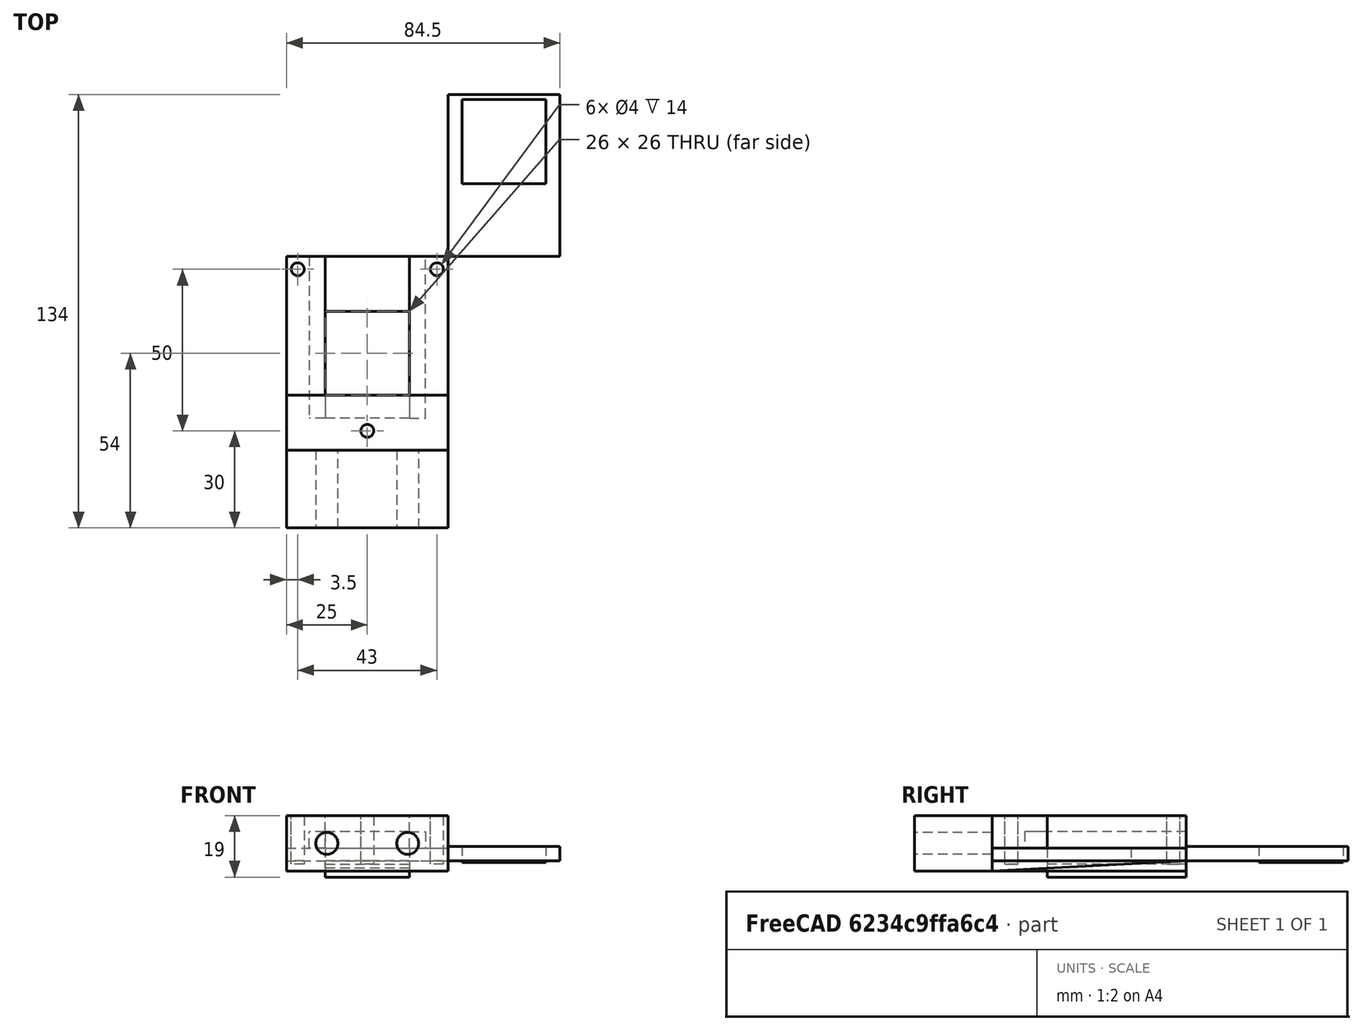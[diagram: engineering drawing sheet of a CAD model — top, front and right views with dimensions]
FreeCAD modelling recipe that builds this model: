
FCSTD DOCUMENT  (FreeCAD 0.15R4671 (Git))
Label: CageTubeConnector
License: All rights reserved
LicenseURL: http://en.wikipedia.org/wiki/All_rights_reserved
objects: Sketcher::SketchObject×22, PartDesign::Pocket×13, PartDesign::Pad×7, Mesh::Feature×2
note: 62 computed .brp shape members not serialized (recipe doc carries the construction recipe); baked Part::Feature solids carry a one-line shape summary decoded from their .brp

FEATURE [Sketcher::SketchObject] Sketch
  sketch-geometry (4):
    g0: LineSegment StartX=-50 StartY=0 StartZ=0 EndX=0 EndY=0 EndZ=0
    g1: LineSegment StartX=0 StartY=0 StartZ=0 EndX=0 EndY=-60 EndZ=0
    g2: LineSegment StartX=0 StartY=-60 StartZ=0 EndX=-50 EndY=-60 EndZ=0
    g3: LineSegment StartX=-50 StartY=-60 StartZ=0 EndX=-50 EndY=0 EndZ=0
  constraints (11):
    c: Coincident(g0,g1)
    c: Coincident(g1,g2)
    c: Coincident(g2,g3)
    c: Coincident(g3,g0)
    c: Horizontal(g0)
    c: Horizontal(g2)
    c: Vertical(g1)
    c: Vertical(g3)
    c: Distance(g0) = 50
    c: Distance(g1) = 60
    c: Coincident(g0,g-1)
FEATURE [PartDesign::Pad] Pad
  Length = 4
  Length2 = 100
  Sketch = -> Sketch
  Type = 0
FEATURE [Sketcher::SketchObject] Sketch001
  Placement = pos=(0,0,4) rot=(0,0,1;0rad)
  Support = -> Pad [Face6]
  sketch-geometry (4):
    g0: LineSegment StartX=-38 StartY=-17 StartZ=0 EndX=-12 EndY=-17 EndZ=0
    g1: LineSegment StartX=-12 StartY=-17 StartZ=0 EndX=-12 EndY=-43 EndZ=0
    g2: LineSegment StartX=-12 StartY=-43 StartZ=0 EndX=-38 EndY=-43 EndZ=0
    g3: LineSegment StartX=-38 StartY=-43 StartZ=0 EndX=-38 EndY=-17 EndZ=0
  constraints (12):
    c: Coincident(g0,g1)
    c: Coincident(g1,g2)
    c: Coincident(g2,g3)
    c: Coincident(g3,g0)
    c: Horizontal(g0)
    c: Horizontal(g2)
    c: Vertical(g1)
    c: Vertical(g3)
    c: Distance(g0) = 26
    c: DistanceX(g-1,g0) = -12
    c: Distance(g3) = 26
    c: DistanceY(g-1,g0) = -17
FEATURE [PartDesign::Pocket] Pocket
  Length = 5
  Sketch = -> Sketch001
  Type = 0
FEATURE [Sketcher::SketchObject] Sketch002
  Placement = pos=(0,0,4) rot=(0,0,1;0rad)
  Support = -> Pocket [Face5]
FEATURE [Sketcher::SketchObject] Sketch003
  Placement = pos=(0,0,4) rot=(0,0,1;0rad)
  Support = -> Pocket [Face5]
  sketch-geometry (4):
    g0: LineSegment StartX=-50 StartY=-43 StartZ=0 EndX=0 EndY=-43 EndZ=0
    g1: LineSegment StartX=0 StartY=-43 StartZ=0 EndX=0 EndY=-60 EndZ=0
    g2: LineSegment StartX=0 StartY=-60 StartZ=0 EndX=-50 EndY=-60 EndZ=0
    g3: LineSegment StartX=-50 StartY=-60 StartZ=0 EndX=-50 EndY=-43 EndZ=0
  constraints (12):
    c: Coincident(g0,g1)
    c: Coincident(g1,g2)
    c: Coincident(g2,g3)
    c: Coincident(g3,g0)
    c: Horizontal(g0)
    c: Horizontal(g2)
    c: Vertical(g1)
    c: Vertical(g3)
    c: Distance(g0) = 50
    c: Distance(g3) = 17
    c: DistanceX(g-1,g0) = 0
    c: DistanceY(g-1,g0) = -43
FEATURE [PartDesign::Pad] Pad001
  Length = 10
  Length2 = 100
  Sketch = -> Sketch003
  Type = 0
FEATURE [Sketcher::SketchObject] Sketch004
  Placement = pos=(0,0,4) rot=(0,0,1;0rad)
  Support = -> Pad001 [Face5]
  sketch-geometry (4):
    g0: LineSegment StartX=-50 StartY=0 StartZ=0 EndX=-38 EndY=0 EndZ=0
    g1: LineSegment StartX=-38 StartY=0 StartZ=0 EndX=-38 EndY=-43 EndZ=0
    g2: LineSegment StartX=-38 StartY=-43 StartZ=0 EndX=-50 EndY=-43 EndZ=0
    g3: LineSegment StartX=-50 StartY=-43 StartZ=0 EndX=-50 EndY=0 EndZ=0
  constraints (12):
    c: Coincident(g0,g1)
    c: Coincident(g1,g2)
    c: Coincident(g2,g3)
    c: Coincident(g3,g0)
    c: Horizontal(g0)
    c: Horizontal(g2)
    c: Vertical(g1)
    c: Vertical(g3)
    c: Distance(g1) = 43
    c: Distance(g0) = 12
    c: DistanceX(g-1,g0) = -38
    c: DistanceY(g0) = 0
FEATURE [PartDesign::Pad] Pad002
  Length = 10
  Length2 = 100
  Sketch = -> Sketch004
  Type = 0
FEATURE [Sketcher::SketchObject] Sketch005
  Placement = pos=(0,0,4) rot=(0,0,1;0rad)
  Support = -> Pad002 [Face11]
  sketch-geometry (4):
    g0: LineSegment StartX=-12 StartY=0 StartZ=0 EndX=0 EndY=0 EndZ=0
    g1: LineSegment StartX=0 StartY=0 StartZ=0 EndX=0 EndY=-43 EndZ=0
    g2: LineSegment StartX=0 StartY=-43 StartZ=0 EndX=-12 EndY=-43 EndZ=0
    g3: LineSegment StartX=-12 StartY=-43 StartZ=0 EndX=-12 EndY=0 EndZ=0
  constraints (12):
    c: Coincident(g0,g1)
    c: Coincident(g1,g2)
    c: Coincident(g2,g3)
    c: Coincident(g3,g0)
    c: Horizontal(g0)
    c: Horizontal(g2)
    c: Vertical(g1)
    c: Vertical(g3)
    c: Distance(g1) = 43
    c: Distance(g0) = 12
    c: DistanceX(g-1,g0) = 0
    c: DistanceY(g-1,g0) = 0
FEATURE [PartDesign::Pad] Pad003
  Length = 10
  Length2 = 100
  Sketch = -> Sketch005
  Type = 0
FEATURE [Sketcher::SketchObject] Sketch006
  Placement = pos=(-38,0,0) rot=(0.57735,0.57735,0.57735;2.0944rad)
  Support = -> Pad003 [Face18]
  sketch-geometry (4):
    g0: LineSegment StartX=0 StartY=9 StartZ=0 EndX=-50 EndY=9 EndZ=0
    g1: LineSegment StartX=-50 StartY=9 StartZ=0 EndX=-50 EndY=4 EndZ=0
    g2: LineSegment StartX=-50 StartY=4 StartZ=0 EndX=0 EndY=4 EndZ=0
    g3: LineSegment StartX=0 StartY=4 StartZ=0 EndX=0 EndY=9 EndZ=0
  constraints (12):
    c: Coincident(g0,g1)
    c: Coincident(g1,g2)
    c: Coincident(g2,g3)
    c: Coincident(g3,g0)
    c: Horizontal(g0)
    c: Horizontal(g2)
    c: Vertical(g1)
    c: Vertical(g3)
    c: Distance(g3) = 5
    c: Distance(g0) = 50
    c: DistanceX(g-1,g2) = 0
    c: DistanceY(g-1,g2) = 4
FEATURE [PartDesign::Pocket] Pocket001
  Length = 5
  Sketch = -> Sketch006
  Type = 0
FEATURE [Sketcher::SketchObject] Sketch007
  Placement = pos=(-12,0,0) rot=(0.57735,-0.57735,-0.57735;2.0944rad)
  Support = -> Pocket001 [Face20]
  sketch-geometry (4):
    g0: LineSegment StartX=0 StartY=4 StartZ=0 EndX=50 EndY=4 EndZ=0
    g1: LineSegment StartX=50 StartY=4 StartZ=0 EndX=50 EndY=9 EndZ=0
    g2: LineSegment StartX=50 StartY=9 StartZ=0 EndX=0 EndY=9 EndZ=0
    g3: LineSegment StartX=0 StartY=9 StartZ=0 EndX=0 EndY=4 EndZ=0
  constraints (12):
    c: Coincident(g0,g1)
    c: Coincident(g1,g2)
    c: Coincident(g2,g3)
    c: Coincident(g3,g0)
    c: Horizontal(g0)
    c: Horizontal(g2)
    c: Vertical(g1)
    c: Vertical(g3)
    c: Distance(g3) = 5
    c: Distance(g2) = 50
    c: DistanceY(g-1,g0) = 4
    c: DistanceX(g-1,g0) = 0
FEATURE [PartDesign::Pocket] Pocket002
  Length = 5
  Sketch = -> Sketch007
  Type = 0
FEATURE [Sketcher::SketchObject] Sketch008
  Placement = pos=(0,-43,0) rot=(0,0.707107,0.707107;3.14159rad)
  Support = -> Pocket002 [Face20]
  sketch-geometry (4):
    g0: LineSegment StartX=38 StartY=4 StartZ=0 EndX=12 EndY=4 EndZ=0
    g1: LineSegment StartX=12 StartY=4 StartZ=0 EndX=12 EndY=9 EndZ=0
    g2: LineSegment StartX=12 StartY=9 StartZ=0 EndX=38 EndY=9 EndZ=0
    g3: LineSegment StartX=38 StartY=9 StartZ=0 EndX=38 EndY=4 EndZ=0
  constraints (12):
    c: Coincident(g0,g1)
    c: Coincident(g1,g2)
    c: Coincident(g2,g3)
    c: Coincident(g3,g0)
    c: Horizontal(g0)
    c: Horizontal(g2)
    c: Vertical(g1)
    c: Vertical(g3)
    c: Distance(g3) = 5
    c: Distance(g0) = 26
    c: DistanceY(g-1,g0) = 4
    c: DistanceX(g-1,g0) = 12
FEATURE [PartDesign::Pocket] Pocket003
  Length = 7
  Sketch = -> Sketch008
  Type = 0
FEATURE [Sketcher::SketchObject] Sketch009
  Placement = pos=(0,0,14) rot=(0,0,1;0rad)
  Support = -> Pocket003 [Face31]
  sketch-geometry (1):
    g0: Circle CenterX=-25 CenterY=-54 CenterZ=0 NormalX=0 NormalY=0 NormalZ=1 Radius=2
  constraints (3):
    c: DistanceX(g-1,g0) = -25
    c: DistanceY(g-1,g0) = -54
    c: Radius(g0) = 2
FEATURE [PartDesign::Pocket] Pocket004
  Length = 15
  Sketch = -> Sketch009
  Type = 0
FEATURE [Sketcher::SketchObject] Sketch010
  Placement = pos=(0,0,14) rot=(0,0,1;0rad)
  Support = -> Pocket004 [Face26]
  sketch-geometry (1):
    g0: Circle CenterX=-46.5 CenterY=-4 CenterZ=0 NormalX=0 NormalY=0 NormalZ=1 Radius=2
  constraints (3):
    c: Radius(g0) = 2
    c: DistanceY(g-1,g0) = -4
    c: DistanceX(g-1,g0) = -46.5
FEATURE [PartDesign::Pocket] Pocket005
  Length = 15
  Sketch = -> Sketch010
  Type = 0
FEATURE [Sketcher::SketchObject] Sketch011
  Placement = pos=(0,0,14) rot=(0,0,1;0rad)
  Support = -> Pocket005 [Face31]
  sketch-geometry (1):
    g0: Circle CenterX=-3.5 CenterY=-4 CenterZ=0 NormalX=0 NormalY=0 NormalZ=1 Radius=2
  constraints (3):
    c: Radius(g0) = 2
    c: DistanceY(g-1,g0) = -4
    c: DistanceX(g-1,g0) = -3.5
FEATURE [PartDesign::Pocket] Pocket006
  Length = 15
  Sketch = -> Sketch011
  Type = 0
FEATURE [Sketcher::SketchObject] Sketch012
  sketch-geometry (4):
    g0: LineSegment StartX=0 StartY=0 StartZ=0 EndX=34.5 EndY=0 EndZ=0
    g1: LineSegment StartX=34.5 StartY=0 StartZ=0 EndX=34.5 EndY=50 EndZ=0
    g2: LineSegment StartX=34.5 StartY=50 StartZ=0 EndX=0 EndY=50 EndZ=0
    g3: LineSegment StartX=0 StartY=50 StartZ=0 EndX=0 EndY=0 EndZ=0
  constraints (11):
    c: Coincident(g0,g1)
    c: Coincident(g1,g2)
    c: Coincident(g2,g3)
    c: Coincident(g3,g0)
    c: Horizontal(g0)
    c: Horizontal(g2)
    c: Vertical(g1)
    c: Vertical(g3)
    c: Coincident(g0,g-1)
    c: Distance(g2) = 34.5
    c: Distance(g3) = 50
FEATURE [PartDesign::Pad] Pad004
  Length = 4.5
  Length2 = 100
  Sketch = -> Sketch012
  Type = 0
FEATURE [Sketcher::SketchObject] Sketch013
  Placement = pos=(0,0,4.5) rot=(0,0,1;0rad)
  Support = -> Pad004 [Face6]
  sketch-geometry (4):
    g0: LineSegment StartX=4.25 StartY=48.5 StartZ=0 EndX=30.25 EndY=48.5 EndZ=0
    g1: LineSegment StartX=30.25 StartY=48.5 StartZ=0 EndX=30.25 EndY=22.5 EndZ=0
    g2: LineSegment StartX=30.25 StartY=22.5 StartZ=0 EndX=4.25 EndY=22.5 EndZ=0
    g3: LineSegment StartX=4.25 StartY=22.5 StartZ=0 EndX=4.25 EndY=48.5 EndZ=0
  constraints (12):
    c: Coincident(g0,g1)
    c: Coincident(g1,g2)
    c: Coincident(g2,g3)
    c: Coincident(g3,g0)
    c: Horizontal(g0)
    c: Horizontal(g2)
    c: Vertical(g1)
    c: Vertical(g3)
    c: Distance(g0) = 26
    c: Distance(g3) = 26
    c: DistanceY(g-1,g0) = 48.5
    c: DistanceX(g-1,g2) = 4.25
FEATURE [PartDesign::Pocket] Pocket007
  Length = 5
  Sketch = -> Sketch013
  Type = 0
FEATURE [Sketcher::SketchObject] Sketch014
  Placement = pos=(0,0,4) rot=(0,0,1;0rad)
  Support = -> Pocket006 [Face16]
  sketch-geometry (4):
    g0: LineSegment StartX=-38 StartY=0 StartZ=0 EndX=-12 EndY=0 EndZ=0
    g1: LineSegment StartX=-12 StartY=0 StartZ=0 EndX=-12 EndY=-17 EndZ=0
    g2: LineSegment StartX=-12 StartY=-17 StartZ=0 EndX=-38 EndY=-17 EndZ=0
    g3: LineSegment StartX=-38 StartY=-17 StartZ=0 EndX=-38 EndY=0 EndZ=0
  constraints (12):
    c: Coincident(g0,g1)
    c: Coincident(g1,g2)
    c: Coincident(g2,g3)
    c: Coincident(g3,g0)
    c: Horizontal(g0)
    c: Horizontal(g2)
    c: Vertical(g1)
    c: Vertical(g3)
    c: Distance(g0) = 26
    c: Distance(g1) = 17
    c: DistanceY(g-1,g0) = 0
    c: DistanceX(g-1,g0) = -12
FEATURE [PartDesign::Pocket] Pocket008
  Length = 5
  Sketch = -> Sketch014
  Type = 0
FEATURE [Sketcher::SketchObject] Sketch015
  Placement = pos=(0,0,0) rot=(1,0,0;3.14159rad)
  Support = -> Pocket008 [Face1]
  sketch-geometry (4):
    g0: LineSegment StartX=-50 StartY=60 StartZ=0 EndX=0 EndY=60 EndZ=0
    g1: LineSegment StartX=0 StartY=60 StartZ=0 EndX=0 EndY=0 EndZ=0
    g2: LineSegment StartX=0 StartY=0 StartZ=0 EndX=-50 EndY=0 EndZ=0
    g3: LineSegment StartX=-50 StartY=0 StartZ=0 EndX=-50 EndY=60 EndZ=0
  constraints (12):
    c: Coincident(g0,g1)
    c: Coincident(g1,g2)
    c: Coincident(g2,g3)
    c: Coincident(g3,g0)
    c: Horizontal(g0)
    c: Horizontal(g2)
    c: Vertical(g1)
    c: Vertical(g3)
    c: PointOnObject(g1,g-1)
    c: Distance(g0) = 50
    c: Distance(g3) = 60
    c: DistanceX(g-1,g1) = 0
FEATURE [PartDesign::Pad] Pad005
  Length = 3.1445
  Length2 = 100
  Sketch = -> Sketch015
  Type = 0
FEATURE [Sketcher::SketchObject] Sketch016
  Placement = pos=(-50,0,0) rot=(0.57735,-0.57735,-0.57735;2.0944rad)
  Support = -> Pad005 [Face18]
  sketch-geometry (3):
    g0: LineSegment StartX=0 StartY=0 StartZ=0 EndX=60 EndY=-3.1445 EndZ=0
    g1: LineSegment StartX=60 StartY=-3.1445 StartZ=0 EndX=60 EndY=0 EndZ=0
    g2: LineSegment StartX=60 StartY=0 StartZ=0 EndX=0 EndY=0 EndZ=0
  constraints (8):
    c: Coincident(g0,g-1)
    c: Coincident(g1,g0)
    c: Coincident(g2,g1)
    c: Coincident(g2,g-1)
    c: Horizontal(g2)
    c: Distance(g1) = 3.1445
    c: Distance(g2) = 60
    c: Angle(g2,g1) = 1.5708
FEATURE [Sketcher::SketchObject] Sketch017
  Placement = pos=(-50,0,0) rot=(0.57735,-0.57735,-0.57735;2.0944rad)
  Support = -> Pad005 [Face18]
  sketch-geometry (3):
    g0: LineSegment StartX=0 StartY=0 StartZ=0 EndX=0 EndY=-3.1445 EndZ=0
    g1: LineSegment StartX=0 StartY=-3.1445 StartZ=0 EndX=60 EndY=-3.1445 EndZ=0
    g2: LineSegment StartX=60 StartY=-3.1445 StartZ=0 EndX=0 EndY=0 EndZ=0
  constraints (8):
    c: Coincident(g0,g-1)
    c: Coincident(g1,g0)
    c: Horizontal(g1)
    c: Coincident(g2,g1)
    c: Coincident(g2,g-1)
    c: Distance(g0) = 3.1445
    c: Distance(g1) = 60
    c: Angle(g1,g0) = 1.5708
FEATURE [PartDesign::Pocket] Pocket009
  Length = 50
  Sketch = -> Sketch017
  Type = 0
FEATURE [Sketcher::SketchObject] Sketch018
  Support = -> Pocket009 [Face32]
  sketch-geometry (4):
    g0: LineSegment StartX=-38 StartY=0 StartZ=0 EndX=-12 EndY=0 EndZ=0
    g1: LineSegment StartX=-12 StartY=0 StartZ=0 EndX=-12 EndY=-43 EndZ=0
    g2: LineSegment StartX=-12 StartY=-43 StartZ=0 EndX=-38 EndY=-43 EndZ=0
    g3: LineSegment StartX=-38 StartY=-43 StartZ=0 EndX=-38 EndY=0 EndZ=0
  constraints (12):
    c: Coincident(g0,g1)
    c: Coincident(g1,g2)
    c: Coincident(g2,g3)
    c: Coincident(g3,g0)
    c: Horizontal(g0)
    c: Horizontal(g2)
    c: Vertical(g1)
    c: Vertical(g3)
    c: Distance(g0) = 26
    c: Distance(g1) = 43
    c: DistanceX(g-1,g0) = -12
    c: DistanceY(g-1,g0) = 0
FEATURE [PartDesign::Pocket] Pocket010
  Length = 5
  Sketch = -> Sketch018
  Type = 0
FEATURE [Sketcher::SketchObject] Sketch019
  Placement = pos=(0,-60,0) rot=(1,0,0;1.5708rad)
  Support = -> Pocket010 [Face1]
  sketch-geometry (4):
    g0: LineSegment StartX=-50 StartY=14 StartZ=0 EndX=0 EndY=14 EndZ=0
    g1: LineSegment StartX=0 StartY=14 StartZ=0 EndX=0 EndY=-3.1445 EndZ=0
    g2: LineSegment StartX=0 StartY=-3.1445 StartZ=0 EndX=-50 EndY=-3.1445 EndZ=0
    g3: LineSegment StartX=-50 StartY=-3.1445 StartZ=0 EndX=-50 EndY=14 EndZ=0
  constraints (12):
    c: Coincident(g0,g1)
    c: Coincident(g1,g2)
    c: Coincident(g2,g3)
    c: Coincident(g3,g0)
    c: Horizontal(g0)
    c: Horizontal(g2)
    c: Vertical(g1)
    c: Vertical(g3)
    c: Distance(g0) = 50
    c: Distance(g3) = 17.1445
    c: DistanceX(g-1,g1) = 0
    c: DistanceY(g-1,g1) = -3.1445
FEATURE [PartDesign::Pad] Pad006
  Length = 24
  Length2 = 100
  Sketch = -> Sketch019
  Type = 0
FEATURE [Sketcher::SketchObject] Sketch020
  Placement = pos=(0,-84,0) rot=(1,0,0;1.5708rad)
  Support = -> Pad006 [Face29]
  sketch-geometry (1):
    g0: Circle CenterX=-37.5 CenterY=5.4277 CenterZ=0 NormalX=0 NormalY=0 NormalZ=1 Radius=3.4
  constraints (3):
    c: DistanceY(g-1,g0) = 5.4277
    c: DistanceX(g-1,g0) = -37.5
    c: Radius(g0) = 3.4
FEATURE [PartDesign::Pocket] Pocket011
  Length = 24
  Sketch = -> Sketch020
  Type = 0
FEATURE [Sketcher::SketchObject] Sketch021
  Placement = pos=(0,-84,0) rot=(1,0,0;1.5708rad)
  Support = -> Pocket011 [Face29]
  sketch-geometry (1):
    g0: Circle CenterX=-12.5 CenterY=5.4277 CenterZ=0 NormalX=0 NormalY=0 NormalZ=1 Radius=3.4
  constraints (3):
    c: Radius(g0) = 3.4
    c: DistanceY(g-1,g0) = 5.4277
    c: DistanceX(g-1,g0) = -12.5
FEATURE [PartDesign::Pocket] Pocket012
  Length = 24
  Sketch = -> Sketch021
  Type = 0
FEATURE [Mesh::Feature] Mesh  label="HomeCageTubeConnector_female"
FEATURE [Mesh::Feature] Mesh001  label="HomeCageTubeConnector_male"
